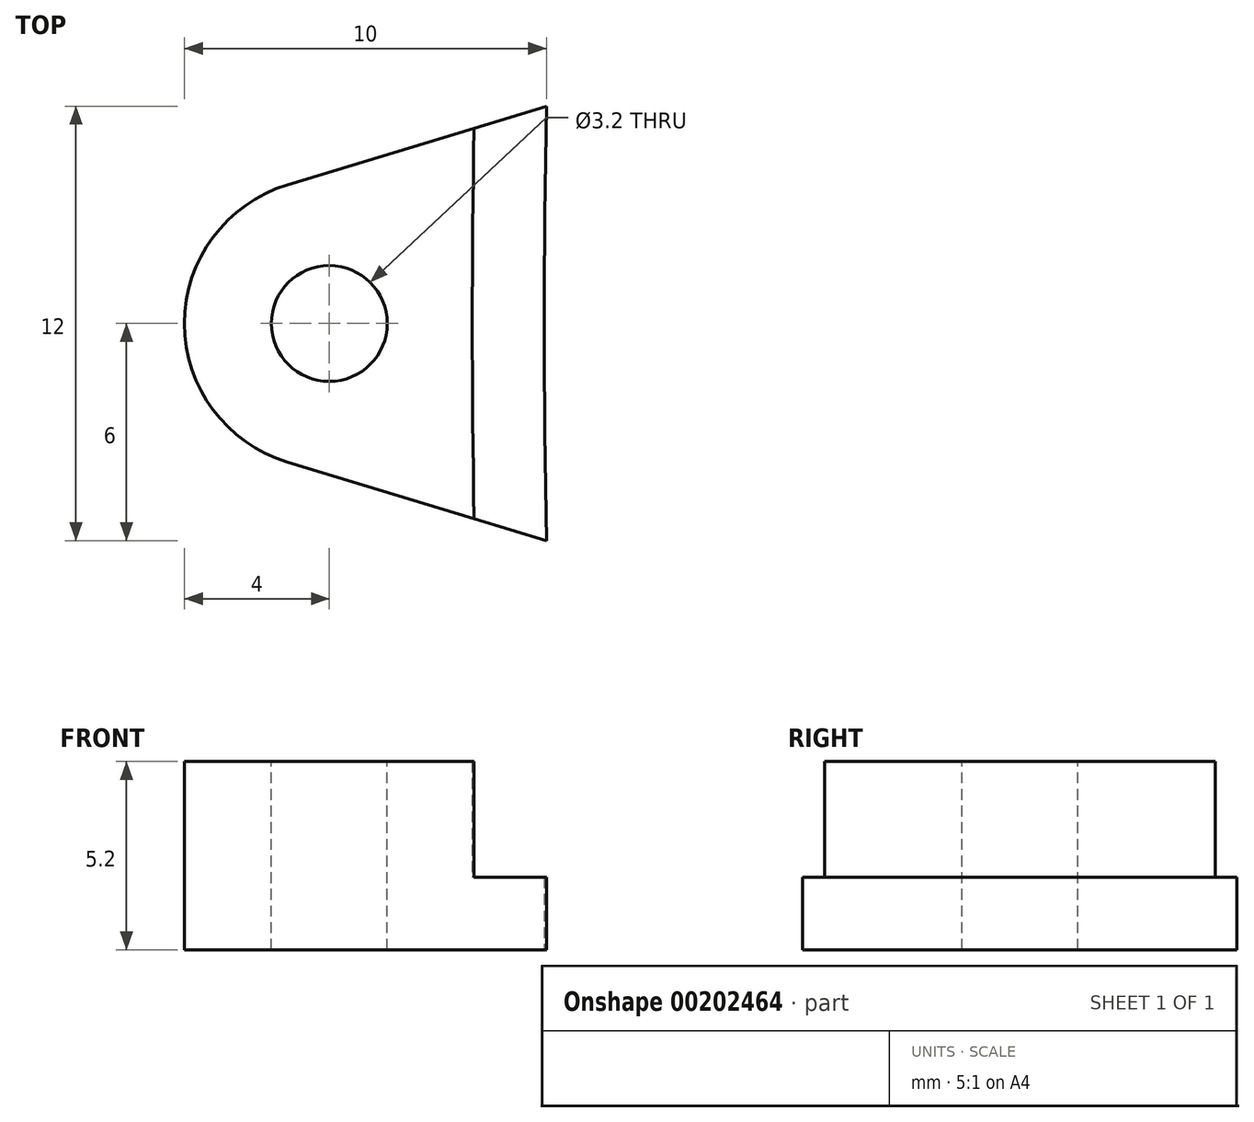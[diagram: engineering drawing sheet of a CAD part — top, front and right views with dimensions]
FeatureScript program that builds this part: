
annotation { "Feature Type Name" : "Feature", "Feature Type Description" : "" }
export const myFeature = defineFeature(function(context is Context, id is Id, definition is map)
    precondition{}
    {
        {
            var Q0;
            Q0=qCreatedBy(makeId("Top.planeOp"),FACE);
            var sketch = newSketch(context, id + "F0", { "sketchPlane" : qUnion([Q0])});
            skArc(sketch, "E0", {"start": v(-1.16, 3.83) * mm, "mid": v(-4, 0) * mm, "end": v(-1.16, -3.83) * mm});
            skArc(sketch, "E1", {"start": v(6, 6) * mm, "mid": v(5.94, 0) * mm, "end": v(6, -6) * mm});
            skLineSegment(sketch, "E2", {"start": v(6, 6) * mm, "end": v(-1.16, 3.83) * mm});
            skLineSegment(sketch, "E3", {"start": v(6, -6) * mm, "end": v(-1.16, -3.83) * mm});
            skSolve(sketch);
        }
        {
            var Q0;
            Q0=makeQuery(id+"F0.imprint","IMPRINT",FACE,{"disambiguationData":[TD([[makeQuery(id+"F0.imprint","IMPRINT",EDGE,{"derivedFrom":sQuery(id+"F0.wireOp",EDGE,"E0")}),1.0]])]});
            extrude(context, id + "F1", {"entities" : qUnion([Q0]), "depth" : 2 * mm});
        }
        {
            var Q0;
            Q0=makeQuery(id+"F1.opExtrude","CAP_FACE",FACE,{"disambiguationData":[OSD([sQuery(id+"F0.wireOp",EDGE,"E0"),sQuery(id+"F0.wireOp",EDGE,"E1"),sQuery(id+"F0.wireOp",EDGE,"E2"),sQuery(id+"F0.wireOp",EDGE,"E3")])],"isStart":false});
            var sketch = newSketch(context, id + "F2", { "sketchPlane" : qUnion([Q0])});
            skArc(sketch, "E4.1", {"start": v(-1.16, 3.83) * mm, "mid": v(-4, 0) * mm, "end": v(-1.16, -3.83) * mm});
            skArc(sketch, "E5", {"start": v(4, 5.4) * mm, "mid": v(3.95, 0) * mm, "end": v(4, -5.4) * mm});
            skLineSegment(sketch, "E6", {"start": v(-1.16, 3.83) * mm, "end": v(4, 5.4) * mm});
            skLineSegment(sketch, "E7", {"start": v(-1.16, -3.83) * mm, "end": v(4, -5.4) * mm});
            skSolve(sketch);
        }
        {
            var Q0;
            Q0=qSketchRegion(id+"F2",true);
            extrude(context, id + "F3", {"entities" : qUnion([Q0]), "operationType" : NewBodyOperationType.ADD, "depth" : 3.2 * mm});
        }
        {
            var Q0;
            Q0=makeQuery(id+"F3.opExtrude","CAP_FACE",FACE,{"disambiguationData":[OSD([sQuery(id+"F2.wireOp",EDGE,"E4.1"),sQuery(id+"F2.wireOp",EDGE,"E5"),sQuery(id+"F2.wireOp",EDGE,"E6"),sQuery(id+"F2.wireOp",EDGE,"E7")])],"isStart":false});
            var sketch = newSketch(context, id + "F4", { "sketchPlane" : qUnion([Q0])});
            skCircle(sketch, "E8", {"center": v(0, 0) * mm, "radius": 1.6 * mm});
            skSolve(sketch);
        }
        {
            var Q0;
            Q0=qSketchRegion(id+"F4",true);
            extrude(context, id + "F5", {"entities" : qUnion([Q0]), "operationType" : NewBodyOperationType.REMOVE, "endBound" : BoundingType.THROUGH_ALL, "oppositeDirection" : true, "depth" : 25 * mm});
        }
    });
